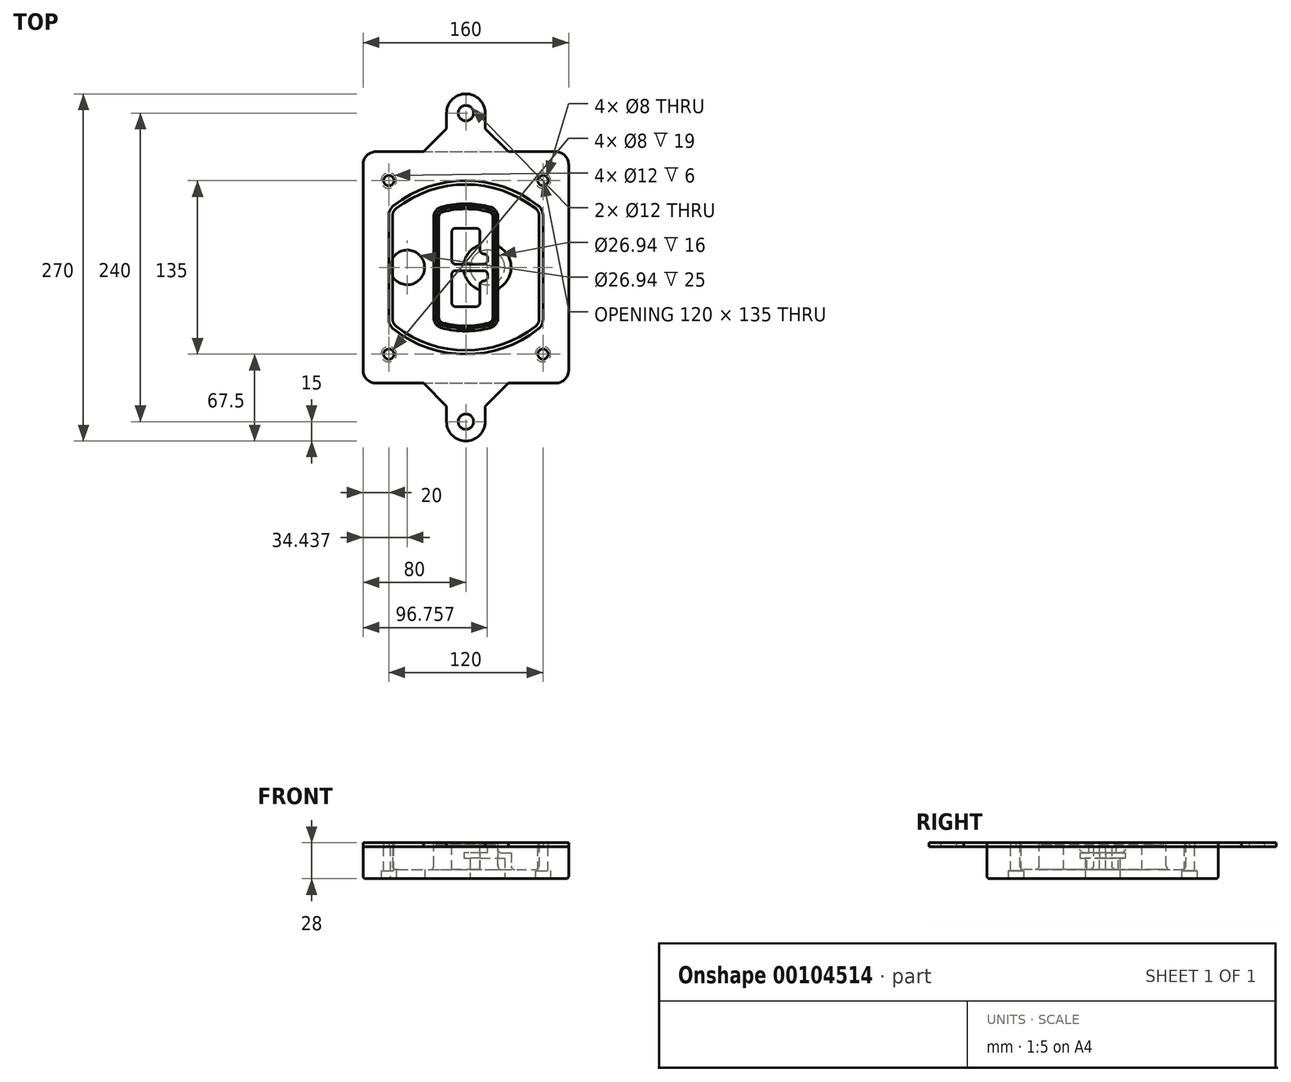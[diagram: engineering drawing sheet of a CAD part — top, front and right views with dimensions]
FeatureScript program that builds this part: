
annotation { "Feature Type Name" : "Feature", "Feature Type Description" : "" }
export const myFeature = defineFeature(function(context is Context, id is Id, definition is map)
    precondition{}
    {
        {
            var Q0;
            Q0=qCreatedBy(makeId("Top.planeOp"),FACE);
            var sketch = newSketch(context, id + "F0", { "sketchPlane" : qUnion([Q0])});
            skPoint(sketch, "E0.rect.middle", {"position": v(0, 0) * mm});
            skLineSegment(sketch, "E1.bottom", {"start": v(-70, -90) * mm, "end": v(70, -90) * mm});
            skLineSegment(sketch, "E1.top", {"start": v(-70, 90) * mm, "end": v(70, 90) * mm});
            skLineSegment(sketch, "E1.left", {"start": v(-80, -80) * mm, "end": v(-80, 80) * mm});
            skLineSegment(sketch, "E1.right", {"start": v(80, -80) * mm, "end": v(80, 80) * mm});
            skLineSegment(sketch, "E2", {"start": v(-80, 90) * mm, "end": v(80, -90) * mm, "construction": true});
            skLineSegment(sketch, "E3", {"start": v(80, 90) * mm, "end": v(-80, -90) * mm, "construction": true});
            skCircle(sketch, "E4", {"center": v(-60, 67.5) * mm, "radius": 4 * mm});
            skCircle(sketch, "E5", {"center": v(60, 67.5) * mm, "radius": 4 * mm});
            skCircle(sketch, "E6", {"center": v(60, -67.5) * mm, "radius": 4 * mm});
            skCircle(sketch, "E7", {"center": v(-60, -67.5) * mm, "radius": 4 * mm});
            skLineSegment(sketch, "E8", {"start": v(-60, 67.5) * mm, "end": v(60, 67.5) * mm, "construction": true});
            skLineSegment(sketch, "E9", {"start": v(60, 67.5) * mm, "end": v(60, -67.5) * mm, "construction": true});
            skLineSegment(sketch, "E10", {"start": v(60, -67.5) * mm, "end": v(-60, -67.5) * mm, "construction": true});
            skLineSegment(sketch, "E11", {"start": v(-60, -67.5) * mm, "end": v(-60, 67.5) * mm, "construction": true});
            skLineSegment(sketch, "E12", {"start": v(-60, 40.3) * mm, "end": v(-60, -40.3) * mm});
            skLineSegment(sketch, "E13", {"start": v(60, 40.3) * mm, "end": v(60, -40.3) * mm});
            skArc(sketch, "E14", {"start": v(56.15, 48.18) * mm, "mid": v(0, 67.5) * mm, "end": v(-56.15, 48.18) * mm});
            skArc(sketch, "E15", {"start": v(-56.15, -48.18) * mm, "mid": v(0, -67.5) * mm, "end": v(56.15, -48.18) * mm});
            skLineSegment(sketch, "E16", {"start": v(-60, 0) * mm, "end": v(60, 0) * mm, "construction": true});
            skPoint(sketch, "E17.visualSharp", {"position": v(-60, -45) * mm});
            skArc(sketch, "E17.filletArc", {"start": v(-60, -40.3) * mm, "mid": v(-58.99, -44.68) * mm, "end": v(-56.15, -48.18) * mm});
            skPoint(sketch, "E18.visualSharp", {"position": v(-60, 45) * mm});
            skArc(sketch, "E18.filletArc", {"start": v(-56.15, 48.18) * mm, "mid": v(-58.99, 44.68) * mm, "end": v(-60, 40.3) * mm});
            skPoint(sketch, "E19.visualSharp", {"position": v(60, 45) * mm});
            skArc(sketch, "E19.filletArc", {"start": v(60, 40.3) * mm, "mid": v(58.99, 44.68) * mm, "end": v(56.15, 48.18) * mm});
            skPoint(sketch, "E20.visualSharp", {"position": v(60, -45) * mm});
            skArc(sketch, "E20.filletArc", {"start": v(56.15, -48.18) * mm, "mid": v(58.99, -44.68) * mm, "end": v(60, -40.3) * mm});
            skPoint(sketch, "E21.visualSharp", {"position": v(-80, 90) * mm});
            skArc(sketch, "E21.filletArc", {"start": v(-70, 90) * mm, "mid": v(-77.07, 87.07) * mm, "end": v(-80, 80) * mm});
            skPoint(sketch, "E22.visualSharp", {"position": v(80, 90) * mm});
            skArc(sketch, "E22.filletArc", {"start": v(80, 80) * mm, "mid": v(77.07, 87.07) * mm, "end": v(70, 90) * mm});
            skPoint(sketch, "E23.visualSharp", {"position": v(80, -90) * mm});
            skArc(sketch, "E23.filletArc", {"start": v(70, -90) * mm, "mid": v(77.07, -87.07) * mm, "end": v(80, -80) * mm});
            skPoint(sketch, "E24.visualSharp", {"position": v(-80, -90) * mm});
            skArc(sketch, "E24.filletArc", {"start": v(-80, -80) * mm, "mid": v(-77.07, -87.07) * mm, "end": v(-70, -90) * mm});
            skArc(sketch, "E25.0", {"start": v(57, 40.3) * mm, "mid": v(56.3, 43.36) * mm, "end": v(54.3, 45.81) * mm});
            skLineSegment(sketch, "E25.1", {"start": v(57, 40.3) * mm, "end": v(57, -40.3) * mm});
            skArc(sketch, "E25.2", {"start": v(54.3, -45.81) * mm, "mid": v(56.3, -43.36) * mm, "end": v(57, -40.3) * mm});
            skArc(sketch, "E25.3", {"start": v(-54.3, -45.81) * mm, "mid": v(0, -64.5) * mm, "end": v(54.3, -45.81) * mm});
            skArc(sketch, "E25.4", {"start": v(-57, -40.3) * mm, "mid": v(-56.3, -43.36) * mm, "end": v(-54.3, -45.81) * mm});
            skArc(sketch, "E25.5", {"start": v(54.3, 45.81) * mm, "mid": v(0, 64.5) * mm, "end": v(-54.3, 45.81) * mm});
            skLineSegment(sketch, "E25.6", {"start": v(-57, 40.3) * mm, "end": v(-57, -40.3) * mm});
            skArc(sketch, "E25.7", {"start": v(-54.3, 45.81) * mm, "mid": v(-56.3, 43.36) * mm, "end": v(-57, 40.3) * mm});
            skArc(sketch, "E26.0", {"start": v(-58.62, 51.33) * mm, "mid": v(-62.58, 46.43) * mm, "end": v(-64, 40.3) * mm});
            skArc(sketch, "E26.1", {"start": v(58.62, 51.33) * mm, "mid": v(0, 71.5) * mm, "end": v(-58.62, 51.33) * mm});
            skArc(sketch, "E26.2", {"start": v(64, 40.3) * mm, "mid": v(62.58, 46.43) * mm, "end": v(58.62, 51.33) * mm});
            skLineSegment(sketch, "E26.3", {"start": v(64, 40.3) * mm, "end": v(64, -40.3) * mm});
            skArc(sketch, "E26.4", {"start": v(58.62, -51.33) * mm, "mid": v(62.58, -46.43) * mm, "end": v(64, -40.3) * mm});
            skLineSegment(sketch, "E26.5", {"start": v(-64, 40.3) * mm, "end": v(-64, -40.3) * mm});
            skArc(sketch, "E26.6", {"start": v(-58.62, -51.33) * mm, "mid": v(0, -71.5) * mm, "end": v(58.62, -51.33) * mm});
            skArc(sketch, "E26.7", {"start": v(-64, -40.3) * mm, "mid": v(-62.58, -46.43) * mm, "end": v(-58.62, -51.33) * mm});
            skSolve(sketch);
        }
        {
            var Q0;
            Q0=makeQuery(id+"F0.imprint","IMPRINT",FACE,{"disambiguationData":[TD([[makeQuery(id+"F0.imprint","IMPRINT",EDGE,{"derivedFrom":sQuery(id+"F0.wireOp",EDGE,"E1.bottom")}),1.0]])]});
            var Q1;
            Q1=makeQuery(id+"F0.imprint","IMPRINT",FACE,{"disambiguationData":[TD([[makeQuery(id+"F0.imprint","IMPRINT",EDGE,{"derivedFrom":sQuery(id+"F0.wireOp",EDGE,"E12")}),1.0]])]});
            var Q2;
            Q2=makeQuery(id+"F0.imprint","IMPRINT",FACE,{"disambiguationData":[TD([[makeQuery(id+"F0.imprint","IMPRINT",EDGE,{"derivedFrom":sQuery(id+"F0.wireOp",EDGE,"E25.0")}),1.0]])]});
            var Q3;
            Q3=makeQuery(id+"F0.imprint","IMPRINT",FACE,{"disambiguationData":[TD([[makeQuery(id+"F0.imprint","IMPRINT",EDGE,{"derivedFrom":sQuery(id+"F0.wireOp",EDGE,"E12")}),-1.0]])]});
            extrude(context, id + "F1", {"entities" : qUnion([Q0, Q1, Q2, Q3]), "oppositeDirection" : true, "depth" : 25 * mm});
        }
        {
            var Q0;
            Q0=makeQuery(id+"F0.imprint","IMPRINT",FACE,{"disambiguationData":[TD([[makeQuery(id+"F0.imprint","IMPRINT",EDGE,{"derivedFrom":sQuery(id+"F0.wireOp",EDGE,"E12")}),1.0]])]});
            extrude(context, id + "F2", {"entities" : qUnion([Q0]), "operationType" : NewBodyOperationType.ADD, "depth" : 3 * mm});
        }
        {
            var Q0;
            Q0=makeQuery(id+"F0.imprint","IMPRINT",FACE,{"disambiguationData":[TD([[makeQuery(id+"F0.imprint","IMPRINT",EDGE,{"derivedFrom":sQuery(id+"F0.wireOp",EDGE,"E25.0")}),1.0]])]});
            extrude(context, id + "F3", {"entities" : qUnion([Q0]), "operationType" : NewBodyOperationType.REMOVE, "oppositeDirection" : true, "depth" : 18 * mm});
        }
        {
            var Q0;
            Q0=makeQuery(id+"F2.opExtrude","CAP_FACE",FACE,{"disambiguationData":[OSD([sQuery(id+"F0.wireOp",EDGE,"E12"),sQuery(id+"F0.wireOp",EDGE,"E13"),sQuery(id+"F0.wireOp",EDGE,"E14"),sQuery(id+"F0.wireOp",EDGE,"E15"),sQuery(id+"F0.wireOp",EDGE,"E17.filletArc"),sQuery(id+"F0.wireOp",EDGE,"E18.filletArc"),sQuery(id+"F0.wireOp",EDGE,"E19.filletArc"),sQuery(id+"F0.wireOp",EDGE,"E20.filletArc"),sQuery(id+"F0.wireOp",EDGE,"E25.0"),sQuery(id+"F0.wireOp",EDGE,"E25.1"),sQuery(id+"F0.wireOp",EDGE,"E25.2"),sQuery(id+"F0.wireOp",EDGE,"E25.3"),sQuery(id+"F0.wireOp",EDGE,"E25.4"),sQuery(id+"F0.wireOp",EDGE,"E25.5"),sQuery(id+"F0.wireOp",EDGE,"E25.6"),sQuery(id+"F0.wireOp",EDGE,"E25.7")])],"isStart":false});
            var sketch = newSketch(context, id + "F4", { "sketchPlane" : qUnion([Q0])});
            skArc(sketch, "E27.0", {"start": v(-19.08, -46.97) * mm, "mid": v(0, -49.5) * mm, "end": v(19.08, -46.97) * mm});
            skArc(sketch, "E28.0", {"start": v(19.08, 46.97) * mm, "mid": v(0, 49.5) * mm, "end": v(-19.08, 46.97) * mm});
            skLineSegment(sketch, "E29", {"start": v(-25, 39.25) * mm, "end": v(-25, -39.25) * mm});
            skLineSegment(sketch, "E30", {"start": v(25, 39.25) * mm, "end": v(25, -39.25) * mm});
            skLineSegment(sketch, "E31", {"start": v(-25, 45.1) * mm, "end": v(25, 45.1) * mm, "construction": true});
            skLineSegment(sketch, "E32", {"start": v(-25, -45.1) * mm, "end": v(25, -45.1) * mm, "construction": true});
            skPoint(sketch, "E33.visualSharp", {"position": v(-25, 45.1) * mm});
            skArc(sketch, "E33.filletArc", {"start": v(-19.08, 46.97) * mm, "mid": v(-23.35, 44.11) * mm, "end": v(-25, 39.25) * mm});
            skPoint(sketch, "E34.visualSharp", {"position": v(25, 45.1) * mm});
            skArc(sketch, "E34.filletArc", {"start": v(25, 39.25) * mm, "mid": v(23.35, 44.11) * mm, "end": v(19.08, 46.97) * mm});
            skPoint(sketch, "E35.visualSharp", {"position": v(25, -45.1) * mm});
            skArc(sketch, "E35.filletArc", {"start": v(19.08, -46.97) * mm, "mid": v(23.35, -44.11) * mm, "end": v(25, -39.25) * mm});
            skPoint(sketch, "E36.visualSharp", {"position": v(-25, -45.1) * mm});
            skArc(sketch, "E36.filletArc", {"start": v(-25, -39.25) * mm, "mid": v(-23.35, -44.11) * mm, "end": v(-19.08, -46.97) * mm});
            skArc(sketch, "E37.0", {"start": v(54.3, 45.81) * mm, "mid": v(0, 64.5) * mm, "end": v(-54.3, 45.81) * mm});
            skArc(sketch, "E37.1", {"start": v(-54.3, 45.81) * mm, "mid": v(-56.3, 43.36) * mm, "end": v(-57, 40.3) * mm});
            skLineSegment(sketch, "E37.2", {"start": v(-57, 40.3) * mm, "end": v(-57, -40.3) * mm});
            skArc(sketch, "E37.3", {"start": v(-57, -40.3) * mm, "mid": v(-56.3, -43.36) * mm, "end": v(-54.3, -45.81) * mm});
            skArc(sketch, "E37.4", {"start": v(-54.3, -45.81) * mm, "mid": v(0, -64.5) * mm, "end": v(54.3, -45.81) * mm});
            skArc(sketch, "E37.5", {"start": v(54.3, -45.81) * mm, "mid": v(56.3, -43.36) * mm, "end": v(57, -40.3) * mm});
            skLineSegment(sketch, "E37.6", {"start": v(57, 40.3) * mm, "end": v(57, -40.3) * mm});
            skArc(sketch, "E37.7", {"start": v(57, 40.3) * mm, "mid": v(56.3, 43.36) * mm, "end": v(54.3, 45.81) * mm});
            skLineSegment(sketch, "E38.0", {"start": v(23, 39.25) * mm, "end": v(23, -39.25) * mm});
            skArc(sketch, "E38.1", {"start": v(18.56, -45.04) * mm, "mid": v(21.76, -42.9) * mm, "end": v(23, -39.25) * mm});
            skArc(sketch, "E38.2", {"start": v(-18.56, -45.04) * mm, "mid": v(0, -47.5) * mm, "end": v(18.56, -45.04) * mm});
            skArc(sketch, "E38.3", {"start": v(-23, -39.25) * mm, "mid": v(-21.76, -42.9) * mm, "end": v(-18.56, -45.04) * mm});
            skLineSegment(sketch, "E38.4", {"start": v(-23, 39.25) * mm, "end": v(-23, -39.25) * mm});
            skArc(sketch, "E38.5", {"start": v(23, 39.25) * mm, "mid": v(21.76, 42.9) * mm, "end": v(18.56, 45.04) * mm});
            skArc(sketch, "E38.6", {"start": v(-18.56, 45.04) * mm, "mid": v(-21.76, 42.9) * mm, "end": v(-23, 39.25) * mm});
            skArc(sketch, "E38.7", {"start": v(18.56, 45.04) * mm, "mid": v(0, 47.5) * mm, "end": v(-18.56, 45.04) * mm});
            skArc(sketch, "E39.0", {"start": v(21, 39.25) * mm, "mid": v(20.18, 41.68) * mm, "end": v(18.04, 43.1) * mm});
            skLineSegment(sketch, "E39.1", {"start": v(21, 39.25) * mm, "end": v(21, -39.25) * mm});
            skArc(sketch, "E39.2", {"start": v(18.04, -43.1) * mm, "mid": v(20.18, -41.68) * mm, "end": v(21, -39.25) * mm});
            skArc(sketch, "E39.3", {"start": v(-18.04, -43.1) * mm, "mid": v(0, -45.5) * mm, "end": v(18.04, -43.1) * mm});
            skArc(sketch, "E39.4", {"start": v(-21, -39.25) * mm, "mid": v(-20.18, -41.68) * mm, "end": v(-18.04, -43.1) * mm});
            skArc(sketch, "E39.5", {"start": v(18.04, 43.1) * mm, "mid": v(0, 45.5) * mm, "end": v(-18.04, 43.1) * mm});
            skLineSegment(sketch, "E39.6", {"start": v(-21, 39.25) * mm, "end": v(-21, -39.25) * mm});
            skArc(sketch, "E39.7", {"start": v(-18.04, 43.1) * mm, "mid": v(-20.18, 41.68) * mm, "end": v(-21, 39.25) * mm});
            skLineSegment(sketch, "E40", {"start": v(-25, 0) * mm, "end": v(25, 0) * mm, "construction": true});
            skLineSegment(sketch, "E41", {"start": v(-11, 5.5) * mm, "end": v(-11, 27.5) * mm});
            skLineSegment(sketch, "E42", {"start": v(-8, 30.5) * mm, "end": v(8, 30.5) * mm});
            skLineSegment(sketch, "E43", {"start": v(11, 27.5) * mm, "end": v(11, 13.5) * mm});
            skLineSegment(sketch, "E44", {"start": v(14, 10.5) * mm, "end": v(14, 10.5) * mm});
            skLineSegment(sketch, "E45", {"start": v(17, 7.5) * mm, "end": v(17, 5.5) * mm});
            skLineSegment(sketch, "E46", {"start": v(14, 2.5) * mm, "end": v(-8, 2.5) * mm});
            skPoint(sketch, "E47.visualSharp", {"position": v(-11, 30.5) * mm});
            skArc(sketch, "E47.filletArc", {"start": v(-8, 30.5) * mm, "mid": v(-10.12, 29.62) * mm, "end": v(-11, 27.5) * mm});
            skPoint(sketch, "E48.visualSharp", {"position": v(11, 30.5) * mm});
            skArc(sketch, "E48.filletArc", {"start": v(11, 27.5) * mm, "mid": v(10.12, 29.62) * mm, "end": v(8, 30.5) * mm});
            skPoint(sketch, "E49.visualSharp", {"position": v(11, 10.5) * mm});
            skArc(sketch, "E49.filletArc", {"start": v(11, 13.5) * mm, "mid": v(11.88, 11.38) * mm, "end": v(14, 10.5) * mm});
            skPoint(sketch, "E50.visualSharp", {"position": v(17, 10.5) * mm});
            skArc(sketch, "E50.filletArc", {"start": v(17, 7.5) * mm, "mid": v(16.12, 9.62) * mm, "end": v(14, 10.5) * mm});
            skPoint(sketch, "E51.visualSharp", {"position": v(17, 2.5) * mm});
            skArc(sketch, "E51.filletArc", {"start": v(14, 2.5) * mm, "mid": v(16.12, 3.38) * mm, "end": v(17, 5.5) * mm});
            skPoint(sketch, "E52.visualSharp", {"position": v(-11, 2.5) * mm});
            skArc(sketch, "E52.filletArc", {"start": v(-11, 5.5) * mm, "mid": v(-10.12, 3.38) * mm, "end": v(-8, 2.5) * mm});
            skLineSegment(sketch, "E53.0.MirrorCS", {"start": v(14, -2.5) * mm, "end": v(-8, -2.5) * mm});
            skArc(sketch, "E54.0.MirrorCS", {"start": v(-11, -5.5) * mm, "mid": v(-10.12, -3.38) * mm, "end": v(-8, -2.5) * mm});
            skLineSegment(sketch, "E55.0.MirrorCS", {"start": v(-11, -5.5) * mm, "end": v(-11, -27.5) * mm});
            skArc(sketch, "E56.0.MirrorCS", {"start": v(-8, -30.5) * mm, "mid": v(-10.12, -29.62) * mm, "end": v(-11, -27.5) * mm});
            skLineSegment(sketch, "E57.0.MirrorCS", {"start": v(-8, -30.5) * mm, "end": v(8, -30.5) * mm});
            skArc(sketch, "E58.0.MirrorCS", {"start": v(11, -27.5) * mm, "mid": v(10.12, -29.62) * mm, "end": v(8, -30.5) * mm});
            skLineSegment(sketch, "E59.0.MirrorCS", {"start": v(11, -27.5) * mm, "end": v(11, -13.5) * mm});
            skArc(sketch, "E60.0.MirrorCS", {"start": v(11, -13.5) * mm, "mid": v(11.88, -11.38) * mm, "end": v(14, -10.5) * mm});
            skArc(sketch, "E61.0.MirrorCS", {"start": v(17, -7.5) * mm, "mid": v(16.12, -9.62) * mm, "end": v(14, -10.5) * mm});
            skLineSegment(sketch, "E62.0.MirrorCS", {"start": v(17, -7.5) * mm, "end": v(17, -5.5) * mm});
            skArc(sketch, "E63.0.MirrorCS", {"start": v(14, -2.5) * mm, "mid": v(16.12, -3.38) * mm, "end": v(17, -5.5) * mm});
            skSolve(sketch);
        }
        {
            var Q0;
            Q0=makeQuery(id+"F4.imprint","IMPRINT",FACE,{"disambiguationData":[TD([[makeQuery(id+"F4.imprint","IMPRINT",EDGE,{"derivedFrom":sQuery(id+"F4.wireOp",EDGE,"E27.0")}),1.0]])]});
            var Q1;
            Q1=makeQuery(id+"F4.imprint","IMPRINT",FACE,{"disambiguationData":[TD([[makeQuery(id+"F4.imprint","IMPRINT",EDGE,{"derivedFrom":sQuery(id+"F4.wireOp",EDGE,"E38.0")}),-1.0]])]});
            var Q2;
            Q2=makeQuery(id+"F4.imprint","IMPRINT",FACE,{"disambiguationData":[TD([[makeQuery(id+"F4.imprint","IMPRINT",EDGE,{"derivedFrom":sQuery(id+"F4.wireOp",EDGE,"E39.0")}),1.0]])]});
            extrude(context, id + "F5", {"entities" : qUnion([Q0, Q1, Q2]), "operationType" : NewBodyOperationType.ADD, "endBound" : BoundingType.UP_TO_NEXT, "oppositeDirection" : true, "depth" : 25 * mm});
        }
        {
            var Q0;
            Q0=makeQuery(id+"F4.imprint","IMPRINT",FACE,{"disambiguationData":[TD([[makeQuery(id+"F4.imprint","IMPRINT",EDGE,{"derivedFrom":sQuery(id+"F4.wireOp",EDGE,"E38.0")}),-1.0]])]});
            extrude(context, id + "F6", {"entities" : qUnion([Q0]), "operationType" : NewBodyOperationType.REMOVE, "oppositeDirection" : true, "depth" : 2 * mm});
        }
        {
            var Q0;
            Q0=makeQuery(id+"F1.opExtrude","CAP_FACE",FACE,{"disambiguationData":[OSD([sQuery(id+"F0.wireOp",EDGE,"E1.bottom"),sQuery(id+"F0.wireOp",EDGE,"E1.top"),sQuery(id+"F0.wireOp",EDGE,"E1.left"),sQuery(id+"F0.wireOp",EDGE,"E1.right"),sQuery(id+"F0.wireOp",EDGE,"E4"),sQuery(id+"F0.wireOp",EDGE,"E5"),sQuery(id+"F0.wireOp",EDGE,"E6"),sQuery(id+"F0.wireOp",EDGE,"E7"),sQuery(id+"F0.wireOp",EDGE,"E21.filletArc"),sQuery(id+"F0.wireOp",EDGE,"E22.filletArc"),sQuery(id+"F0.wireOp",EDGE,"E23.filletArc"),sQuery(id+"F0.wireOp",EDGE,"E24.filletArc")])],"isStart":false});
            var sketch = newSketch(context, id + "F7", { "sketchPlane" : qUnion([Q0])});
            skCircle(sketch, "E64", {"center": v(16.76, 0) * mm, "radius": 13.47 * mm});
            skCircle(sketch, "E65", {"center": v(-45.56, 0) * mm, "radius": 13.47 * mm});
            skLineSegment(sketch, "E66", {"start": v(80, 0) * mm, "end": v(-80, 0) * mm});
            skCircle(sketch, "E67", {"center": v(16.76, 0) * mm, "radius": 18.47 * mm});
            skCircle(sketch, "E68", {"center": v(60, -67.5) * mm, "radius": 6 * mm});
            skCircle(sketch, "E69", {"center": v(-60, -67.5) * mm, "radius": 6 * mm});
            skCircle(sketch, "E70", {"center": v(-60, 67.5) * mm, "radius": 6 * mm});
            skCircle(sketch, "E71", {"center": v(60, 67.5) * mm, "radius": 6 * mm});
            skSolve(sketch);
        }
        {
            var Q0;
            {var subQ1=sQuery(id+"F7.wireOp",EDGE,"E66");var subQ4=sQuery(id+"F7.wireOp",EDGE,"E64");var subQ6=makeQuery(id+"F7.imprint","INTERSECT",VERTEX,{"disambiguationData":[OD(0.0)],"derivedFrom":[subQ4,subQ1]});Q0=makeQuery(id+"F7.imprint","IMPRINT",FACE,{"disambiguationData":[TD([[makeQuery(id+"F7.imprint","IMPRINT",EDGE,{"disambiguationData":[TD([[subQ6,-1.0]])],"derivedFrom":subQ4}),-1.0]])]});}
            var Q1;
            {var subQ0=sQuery(id+"F7.wireOp",EDGE,"E66");var subQ1=sQuery(id+"F7.wireOp",EDGE,"E64");var subQ3=makeQuery(id+"F7.imprint","INTERSECT",VERTEX,{"disambiguationData":[OD(0.0)],"derivedFrom":[subQ1,subQ0]});Q1=makeQuery(id+"F7.imprint","IMPRINT",FACE,{"disambiguationData":[TD([[makeQuery(id+"F7.imprint","IMPRINT",EDGE,{"disambiguationData":[TD([[subQ3,-1.0]])],"derivedFrom":subQ1}),1.0]])]});}
            var Q2;
            {var subQ0=sQuery(id+"F7.wireOp",EDGE,"E66");var subQ1=sQuery(id+"F7.wireOp",EDGE,"E64");var subQ3=makeQuery(id+"F7.imprint","INTERSECT",VERTEX,{"disambiguationData":[OD(0.0)],"derivedFrom":[subQ1,subQ0]});Q2=makeQuery(id+"F7.imprint","IMPRINT",FACE,{"disambiguationData":[TD([[makeQuery(id+"F7.imprint","IMPRINT",EDGE,{"disambiguationData":[TD([[subQ3,1.0]])],"derivedFrom":subQ1}),1.0]])]});}
            var Q3;
            {var subQ1=sQuery(id+"F7.wireOp",EDGE,"E66");var subQ4=sQuery(id+"F7.wireOp",EDGE,"E64");var subQ6=makeQuery(id+"F7.imprint","INTERSECT",VERTEX,{"disambiguationData":[OD(0.0)],"derivedFrom":[subQ4,subQ1]});Q3=makeQuery(id+"F7.imprint","IMPRINT",FACE,{"disambiguationData":[TD([[makeQuery(id+"F7.imprint","IMPRINT",EDGE,{"disambiguationData":[TD([[subQ6,1.0]])],"derivedFrom":subQ4}),-1.0]])]});}
            extrude(context, id + "F8", {"entities" : qUnion([Q0, Q1, Q2, Q3]), "operationType" : NewBodyOperationType.ADD, "oppositeDirection" : true, "depth" : 20 * mm});
        }
        {
            var Q0;
            {var subQ0=sQuery(id+"F7.wireOp",EDGE,"E66");var subQ1=sQuery(id+"F7.wireOp",EDGE,"E64");var subQ3=makeQuery(id+"F7.imprint","INTERSECT",VERTEX,{"disambiguationData":[OD(0.0)],"derivedFrom":[subQ1,subQ0]});Q0=makeQuery(id+"F7.imprint","IMPRINT",FACE,{"disambiguationData":[TD([[makeQuery(id+"F7.imprint","IMPRINT",EDGE,{"disambiguationData":[TD([[subQ3,-1.0]])],"derivedFrom":subQ1}),1.0]])]});}
            var Q1;
            {var subQ0=sQuery(id+"F7.wireOp",EDGE,"E66");var subQ1=sQuery(id+"F7.wireOp",EDGE,"E64");var subQ3=makeQuery(id+"F7.imprint","INTERSECT",VERTEX,{"disambiguationData":[OD(0.0)],"derivedFrom":[subQ1,subQ0]});Q1=makeQuery(id+"F7.imprint","IMPRINT",FACE,{"disambiguationData":[TD([[makeQuery(id+"F7.imprint","IMPRINT",EDGE,{"disambiguationData":[TD([[subQ3,1.0]])],"derivedFrom":subQ1}),1.0]])]});}
            extrude(context, id + "F9", {"entities" : qUnion([Q0, Q1]), "operationType" : NewBodyOperationType.REMOVE, "oppositeDirection" : true, "depth" : 16 * mm});
        }
        {
            var Q0;
            {var subQ0=sQuery(id+"F7.wireOp",EDGE,"E66");var subQ1=sQuery(id+"F7.wireOp",EDGE,"E65");var subQ3=makeQuery(id+"F7.imprint","INTERSECT",VERTEX,{"disambiguationData":[OD(0.0)],"derivedFrom":[subQ1,subQ0]});Q0=makeQuery(id+"F7.imprint","IMPRINT",FACE,{"disambiguationData":[TD([[makeQuery(id+"F7.imprint","IMPRINT",EDGE,{"disambiguationData":[TD([[subQ3,-1.0]])],"derivedFrom":subQ1}),1.0]])]});}
            var Q1;
            {var subQ0=sQuery(id+"F7.wireOp",EDGE,"E66");var subQ1=sQuery(id+"F7.wireOp",EDGE,"E65");var subQ3=makeQuery(id+"F7.imprint","INTERSECT",VERTEX,{"disambiguationData":[OD(0.0)],"derivedFrom":[subQ1,subQ0]});Q1=makeQuery(id+"F7.imprint","IMPRINT",FACE,{"disambiguationData":[TD([[makeQuery(id+"F7.imprint","IMPRINT",EDGE,{"disambiguationData":[TD([[subQ3,1.0]])],"derivedFrom":subQ1}),1.0]])]});}
            extrude(context, id + "F10", {"entities" : qUnion([Q0, Q1]), "operationType" : NewBodyOperationType.REMOVE, "oppositeDirection" : true, "depth" : 25 * mm});
        }
        {
            var Q0;
            Q0=makeQuery(id+"F7.imprint","IMPRINT",FACE,{"disambiguationData":[TD([[makeQuery(id+"F7.imprint","IMPRINT",EDGE,{"derivedFrom":sQuery(id+"F7.wireOp",EDGE,"E68")}),1.0]])]});
            var Q1;
            Q1=makeQuery(id+"F7.imprint","IMPRINT",FACE,{"disambiguationData":[TD([[makeQuery(id+"F7.imprint","IMPRINT",EDGE,{"derivedFrom":makeQuery(id+"F1.opExtrude","CAP_EDGE",EDGE,{"disambiguationData":[OSD([sQuery(id+"F0.wireOp",EDGE,"E5")])],"isStart":false})}),-1.0]])]});
            var Q2;
            Q2=makeQuery(id+"F7.imprint","IMPRINT",FACE,{"disambiguationData":[TD([[makeQuery(id+"F7.imprint","IMPRINT",EDGE,{"derivedFrom":sQuery(id+"F7.wireOp",EDGE,"E69")}),1.0]])]});
            var Q3;
            Q3=makeQuery(id+"F7.imprint","IMPRINT",FACE,{"disambiguationData":[TD([[makeQuery(id+"F7.imprint","IMPRINT",EDGE,{"derivedFrom":makeQuery(id+"F1.opExtrude","CAP_EDGE",EDGE,{"disambiguationData":[OSD([sQuery(id+"F0.wireOp",EDGE,"E4")])],"isStart":false})}),-1.0]])]});
            var Q4;
            Q4=makeQuery(id+"F7.imprint","IMPRINT",FACE,{"disambiguationData":[TD([[makeQuery(id+"F7.imprint","IMPRINT",EDGE,{"derivedFrom":sQuery(id+"F7.wireOp",EDGE,"E70")}),1.0]])]});
            var Q5;
            Q5=makeQuery(id+"F7.imprint","IMPRINT",FACE,{"disambiguationData":[TD([[makeQuery(id+"F7.imprint","IMPRINT",EDGE,{"derivedFrom":makeQuery(id+"F1.opExtrude","CAP_EDGE",EDGE,{"disambiguationData":[OSD([sQuery(id+"F0.wireOp",EDGE,"E7")])],"isStart":false})}),-1.0]])]});
            var Q6;
            Q6=makeQuery(id+"F7.imprint","IMPRINT",FACE,{"disambiguationData":[TD([[makeQuery(id+"F7.imprint","IMPRINT",EDGE,{"derivedFrom":sQuery(id+"F7.wireOp",EDGE,"E71")}),1.0]])]});
            var Q7;
            Q7=makeQuery(id+"F7.imprint","IMPRINT",FACE,{"disambiguationData":[TD([[makeQuery(id+"F7.imprint","IMPRINT",EDGE,{"derivedFrom":makeQuery(id+"F1.opExtrude","CAP_EDGE",EDGE,{"disambiguationData":[OSD([sQuery(id+"F0.wireOp",EDGE,"E6")])],"isStart":false})}),-1.0]])]});
            extrude(context, id + "F11", {"entities" : qUnion([Q0, Q1, Q2, Q3, Q4, Q5, Q6, Q7]), "operationType" : NewBodyOperationType.REMOVE, "oppositeDirection" : true, "depth" : 6 * mm});
        }
        {
            var Q0;
            Q0=makeQuery(id+"F9.boolean.opBoolean","COPY",FACE,{"derivedFrom":makeQuery(id+"F9.opExtrude","CAP_FACE",FACE,{"disambiguationData":[OSD([sQuery(id+"F7.wireOp",EDGE,"E64")])],"isStart":false})});
            var sketch = newSketch(context, id + "F12", { "sketchPlane" : qUnion([Q0])});
            skArc(sketch, "E72.0", {"start": v(11, 17.55) * mm, "mid": v(2.57, 11.82) * mm, "end": v(-1.54, 2.5) * mm});
            skArc(sketch, "E72.1", {"start": v(-1.54, -2.5) * mm, "mid": v(2.57, -11.82) * mm, "end": v(11, -17.55) * mm});
            skLineSegment(sketch, "E73", {"start": v(-1.54, -2.5) * mm, "end": v(14, -2.5) * mm});
            skLineSegment(sketch, "E74.0", {"start": v(14, 2.5) * mm, "end": v(-1.54, 2.5) * mm});
            skArc(sketch, "E74.1", {"start": v(14, 2.5) * mm, "mid": v(16.12, 3.38) * mm, "end": v(17, 5.5) * mm});
            skLineSegment(sketch, "E74.2", {"start": v(17, 7.5) * mm, "end": v(17, 5.5) * mm});
            skArc(sketch, "E74.3", {"start": v(17, 7.5) * mm, "mid": v(16.12, 9.62) * mm, "end": v(14, 10.5) * mm});
            skArc(sketch, "E74.4", {"start": v(11, 13.5) * mm, "mid": v(11.88, 11.38) * mm, "end": v(14, 10.5) * mm});
            skLineSegment(sketch, "E74.5", {"start": v(11, 17.55) * mm, "end": v(11, 13.5) * mm});
            skLineSegment(sketch, "E74.7", {"start": v(14, -2.5) * mm, "end": v(-1.54, -2.5) * mm});
            skArc(sketch, "E74.8", {"start": v(14, -2.5) * mm, "mid": v(16.12, -3.38) * mm, "end": v(17, -5.5) * mm});
            skLineSegment(sketch, "E74.9", {"start": v(17, -7.5) * mm, "end": v(17, -5.5) * mm});
            skArc(sketch, "E74.10", {"start": v(17, -7.5) * mm, "mid": v(16.12, -9.62) * mm, "end": v(14, -10.5) * mm});
            skArc(sketch, "E74.11", {"start": v(11, -13.5) * mm, "mid": v(11.88, -11.38) * mm, "end": v(14, -10.5) * mm});
            skLineSegment(sketch, "E74.12", {"start": v(11, -17.55) * mm, "end": v(11, -13.5) * mm});
            skPoint(sketch, "E75.orphan", {"position": v(11, -27.5) * mm});
            skPoint(sketch, "E76.orphan", {"position": v(-8, -2.5) * mm});
            skPoint(sketch, "E77.orphan", {"position": v(-8, 2.5) * mm});
            skPoint(sketch, "E78.orphan", {"position": v(11, 27.5) * mm});
            skSolve(sketch);
        }
        {
            var Q0;
            {var subQ7=sQuery(id+"F12.wireOp",EDGE,"E72.0");var subQ14=sQuery(id+"F12.wireOp",EDGE,"E72.1");var subQ16=sQuery(id+"F12.wireOp",EDGE,"E74.1");var subQ18=sQuery(id+"F12.wireOp",EDGE,"E74.8");Q0=qUnion([makeQuery(id+"F12.imprint","IMPRINT",FACE,{"disambiguationData":[TD([[makeQuery(id+"F12.imprint","IMPRINT",EDGE,{"derivedFrom":subQ7}),1.0]])]}),makeQuery(id+"F12.imprint","IMPRINT",FACE,{"disambiguationData":[TD([[makeQuery(id+"F12.imprint","IMPRINT",EDGE,{"derivedFrom":subQ14}),1.0]])]}),makeQuery(id+"F12.imprint","IMPRINT",FACE,{"disambiguationData":[TD([[makeQuery(id+"F12.imprint","IMPRINT",EDGE,{"derivedFrom":subQ16}),1.0]])]}),makeQuery(id+"F12.imprint","IMPRINT",FACE,{"disambiguationData":[TD([[makeQuery(id+"F12.imprint","IMPRINT",EDGE,{"derivedFrom":subQ18}),-1.0]])]})]);}
            var Q1;
            Q1=makeQuery(id+"F5.boolean.opBoolean","SPLIT",FACE,{"disambiguationData":[TD([makeQuery(id+"F5.opExtrude","SWEPT_FACE",FACE,{"disambiguationData":[OSD([sQuery(id+"F4.wireOp",EDGE,"E41")])]})])],"derivedFrom":makeQuery(id+"F3.boolean.opBoolean","COPY",FACE,{"derivedFrom":makeQuery(id+"F3.opExtrude","CAP_FACE",FACE,{"disambiguationData":[OSD([sQuery(id+"F0.wireOp",EDGE,"E25.0"),sQuery(id+"F0.wireOp",EDGE,"E25.1"),sQuery(id+"F0.wireOp",EDGE,"E25.2"),sQuery(id+"F0.wireOp",EDGE,"E25.3"),sQuery(id+"F0.wireOp",EDGE,"E25.4"),sQuery(id+"F0.wireOp",EDGE,"E25.5"),sQuery(id+"F0.wireOp",EDGE,"E25.6"),sQuery(id+"F0.wireOp",EDGE,"E25.7")])],"isStart":false})})});
            extrude(context, id + "F13", {"entities" : qUnion([Q0]), "operationType" : NewBodyOperationType.REMOVE, "endBound" : BoundingType.UP_TO_SURFACE, "endBoundEntityFace" : qUnion([Q1]), "depth" : 25 * mm});
        }
        {
            var Q0;
            Q0=makeQuery(id+"F3.boolean.opBoolean","COPY",EDGE,{"derivedFrom":makeQuery(id+"F3.opExtrude","CAP_EDGE",EDGE,{"disambiguationData":[OSD([sQuery(id+"F0.wireOp",EDGE,"E25.6")])],"isStart":false})});
            var Q1;
            Q1=makeQuery(id+"F8.boolean.opBoolean","INTERSECT",EDGE,{"derivedFrom":[makeQuery(id+"F5.opExtrude","SWEPT_FACE",FACE,{"disambiguationData":[OSD([sQuery(id+"F4.wireOp",EDGE,"E30")])]}),makeQuery(id+"F8.opExtrude","CAP_FACE",FACE,{"disambiguationData":[OSD([sQuery(id+"F7.wireOp",EDGE,"E67")])],"isStart":false})]});
            var Q2;
            Q2=makeQuery(id+"F8.boolean.opBoolean","INTERSECT",EDGE,{"disambiguationData":[OD(1.0)],"derivedFrom":[makeQuery(id+"F5.opExtrude","SWEPT_FACE",FACE,{"disambiguationData":[OSD([sQuery(id+"F4.wireOp",EDGE,"E30")])]}),makeQuery(id+"F8.opExtrude","SWEPT_FACE",FACE,{"disambiguationData":[OSD([sQuery(id+"F7.wireOp",EDGE,"E67")])]})]});
            var Q3;
            {var subQ0=sQuery(id+"F4.wireOp",EDGE,"E30");Q3=makeQuery(id+"F8.boolean.opBoolean","SPLIT",EDGE,{"disambiguationData":[TD([makeQuery(id+"F5.opExtrude","SWEPT_FACE",FACE,{"disambiguationData":[OSD([sQuery(id+"F4.wireOp",EDGE,"E35.filletArc")])]})])],"derivedFrom":makeQuery(id+"F5.opExtrude","CAP_EDGE",EDGE,{"disambiguationData":[OSD([subQ0])],"isStart":false})});}
            var Q4;
            {var subQ0=sQuery(id+"F0.wireOp",EDGE,"E25.7");var subQ1=sQuery(id+"F0.wireOp",EDGE,"E25.1");var subQ2=sQuery(id+"F0.wireOp",EDGE,"E25.6");var subQ3=sQuery(id+"F0.wireOp",EDGE,"E25.5");var subQ4=sQuery(id+"F0.wireOp",EDGE,"E25.4");var subQ5=sQuery(id+"F0.wireOp",EDGE,"E25.0");var subQ6=sQuery(id+"F0.wireOp",EDGE,"E25.2");var subQ7=sQuery(id+"F0.wireOp",EDGE,"E25.3");Q4=makeQuery(id+"F8.boolean.opBoolean","INTERSECT",EDGE,{"derivedFrom":[makeQuery(id+"F5.boolean.opBoolean","SPLIT",FACE,{"disambiguationData":[TD([makeQuery(id+"F2.opExtrude","SWEPT_FACE",FACE,{"disambiguationData":[OSD([subQ5])]})])],"derivedFrom":makeQuery(id+"F3.boolean.opBoolean","COPY",FACE,{"derivedFrom":makeQuery(id+"F3.opExtrude","CAP_FACE",FACE,{"disambiguationData":[OSD([subQ5,subQ1,subQ6,subQ7,subQ4,subQ3,subQ2,subQ0])],"isStart":false})})}),makeQuery(id+"F8.opExtrude","SWEPT_FACE",FACE,{"disambiguationData":[OSD([sQuery(id+"F7.wireOp",EDGE,"E67")])]})]});}
            var Q5;
            Q5=makeQuery(id+"F8.boolean.opBoolean","INTERSECT",EDGE,{"disambiguationData":[OD(0.0)],"derivedFrom":[makeQuery(id+"F5.opExtrude","SWEPT_FACE",FACE,{"disambiguationData":[OSD([sQuery(id+"F4.wireOp",EDGE,"E30")])]}),makeQuery(id+"F8.opExtrude","SWEPT_FACE",FACE,{"disambiguationData":[OSD([sQuery(id+"F7.wireOp",EDGE,"E67")])]})]});
            fillet(context, id + "F14", {"entities" : qUnion([Q0, Q1, Q2, Q3, Q4, Q5]), "radius" : 3 * mm, "tangentPropagation" : true, "allowEdgeOverflow" : false});
        }
        {
            var Q0;
            Q0=makeQuery(id+"F1.opExtrude","CAP_EDGE",EDGE,{"disambiguationData":[OSD([sQuery(id+"F0.wireOp",EDGE,"E1.bottom")])],"isStart":false});
            fillet(context, id + "F15", {"entities" : qUnion([Q0]), "radius" : 2 * mm, "tangentPropagation" : true, "allowEdgeOverflow" : false});
        }
        {
            var Q0;
            {var subQ0=sQuery(id+"F0.wireOp",EDGE,"E22.filletArc");var subQ1=sQuery(id+"F0.wireOp",EDGE,"E7");var subQ2=sQuery(id+"F0.wireOp",EDGE,"E6");var subQ3=sQuery(id+"F0.wireOp",EDGE,"E5");var subQ4=sQuery(id+"F0.wireOp",EDGE,"E4");var subQ5=sQuery(id+"F0.wireOp",EDGE,"E1.bottom");var subQ6=sQuery(id+"F0.wireOp",EDGE,"E21.filletArc");var subQ7=sQuery(id+"F0.wireOp",EDGE,"E1.top");var subQ8=sQuery(id+"F0.wireOp",EDGE,"E1.left");var subQ9=sQuery(id+"F0.wireOp",EDGE,"E1.right");var subQ10=sQuery(id+"F0.wireOp",EDGE,"E23.filletArc");var subQ11=sQuery(id+"F0.wireOp",EDGE,"E24.filletArc");Q0=makeQuery(id+"F2.boolean.opBoolean","SPLIT",FACE,{"disambiguationData":[TD([makeQuery(id+"F1.opExtrude","SWEPT_FACE",FACE,{"disambiguationData":[OSD([subQ5])]})])],"derivedFrom":makeQuery(id+"F1.opExtrude","CAP_FACE",FACE,{"disambiguationData":[OSD([subQ5,subQ7,subQ8,subQ9,subQ4,subQ3,subQ2,subQ1,subQ6,subQ0,subQ10,subQ11])],"isStart":true})});}
            var sketch = newSketch(context, id + "F16", { "sketchPlane" : qUnion([Q0])});
            skSolve(sketch);
        }
        {
            var Q0;
            {var subQ4=sQuery(id+"F0.wireOp",EDGE,"E1.bottom");Q0=makeQuery(id+"F16.imprint","IMPRINT",FACE,{"disambiguationData":[TD([[makeQuery(id+"F16.imprint","IMPRINT",EDGE,{"derivedFrom":makeQuery(id+"F1.opExtrude","CAP_EDGE",EDGE,{"disambiguationData":[OSD([subQ4])],"isStart":true})}),1.0]])]});}
            var sketch = newSketch(context, id + "F17", { "sketchPlane" : qUnion([Q0])});
            skLineSegment(sketch, "E79.0", {"start": v(-80, -80) * mm, "end": v(-80, 80) * mm});
            skArc(sketch, "E79.1", {"start": v(-70, 90) * mm, "mid": v(-77.07, 87.07) * mm, "end": v(-80, 80) * mm});
            skLineSegment(sketch, "E79.2", {"start": v(-70, 90) * mm, "end": v(70, 90) * mm});
            skArc(sketch, "E79.3", {"start": v(80, 80) * mm, "mid": v(77.07, 87.07) * mm, "end": v(70, 90) * mm});
            skLineSegment(sketch, "E79.4", {"start": v(80, -80) * mm, "end": v(80, 80) * mm});
            skArc(sketch, "E79.5", {"start": v(70, -90) * mm, "mid": v(77.07, -87.07) * mm, "end": v(80, -80) * mm});
            skLineSegment(sketch, "E79.6", {"start": v(-70, -90) * mm, "end": v(70, -90) * mm});
            skArc(sketch, "E79.7", {"start": v(-80, -80) * mm, "mid": v(-77.07, -87.07) * mm, "end": v(-70, -90) * mm});
            skCircle(sketch, "E79.8", {"center": v(-60, -67.5) * mm, "radius": 4 * mm});
            skCircle(sketch, "E79.9", {"center": v(60, -67.5) * mm, "radius": 4 * mm});
            skCircle(sketch, "E79.10", {"center": v(60, 67.5) * mm, "radius": 4 * mm});
            skCircle(sketch, "E79.11", {"center": v(-60, 67.5) * mm, "radius": 4 * mm});
            skArc(sketch, "E79.12", {"start": v(56.15, 48.18) * mm, "mid": v(0, 67.5) * mm, "end": v(-56.15, 48.18) * mm});
            skArc(sketch, "E79.13", {"start": v(60, 40.3) * mm, "mid": v(58.99, 44.68) * mm, "end": v(56.15, 48.18) * mm});
            skLineSegment(sketch, "E79.14", {"start": v(60, 40.3) * mm, "end": v(60, -40.3) * mm});
            skArc(sketch, "E79.15", {"start": v(56.15, -48.18) * mm, "mid": v(58.99, -44.68) * mm, "end": v(60, -40.3) * mm});
            skArc(sketch, "E79.16", {"start": v(-56.15, -48.18) * mm, "mid": v(0, -67.5) * mm, "end": v(56.15, -48.18) * mm});
            skArc(sketch, "E79.17", {"start": v(-60, -40.3) * mm, "mid": v(-58.99, -44.68) * mm, "end": v(-56.15, -48.18) * mm});
            skLineSegment(sketch, "E79.18", {"start": v(-60, 40.3) * mm, "end": v(-60, -40.3) * mm});
            skArc(sketch, "E79.19", {"start": v(-56.15, 48.18) * mm, "mid": v(-58.99, 44.68) * mm, "end": v(-60, 40.3) * mm});
            skLineSegment(sketch, "E80", {"start": v(0, 120) * mm, "end": v(0, 90) * mm, "construction": true});
            skLineSegment(sketch, "E81", {"start": v(-33, 90) * mm, "end": v(-15, 108) * mm});
            skLineSegment(sketch, "E82", {"start": v(-15, 108) * mm, "end": v(-15, 120) * mm});
            skLineSegment(sketch, "E83", {"start": v(15, 120) * mm, "end": v(15, 108) * mm});
            skLineSegment(sketch, "E84", {"start": v(15, 108) * mm, "end": v(33, 90) * mm});
            skCircle(sketch, "E85", {"center": v(0, 120) * mm, "radius": 6 * mm});
            skArc(sketch, "E86", {"start": v(15, 120) * mm, "mid": v(0, 135) * mm, "end": v(-15, 120) * mm});
            skLineSegment(sketch, "E87", {"start": v(80, 0) * mm, "end": v(-80, 0) * mm, "construction": true});
            skLineSegment(sketch, "E88.MirrorCS", {"start": v(-33, -90) * mm, "end": v(-15, -108) * mm});
            skLineSegment(sketch, "E89.MirrorCS", {"start": v(-15, -108) * mm, "end": v(-15, -120) * mm});
            skArc(sketch, "E90.MirrorCS", {"start": v(15, -120) * mm, "mid": v(0, -135) * mm, "end": v(-15, -120) * mm});
            skLineSegment(sketch, "E91.MirrorCS", {"start": v(15, -120) * mm, "end": v(15, -108) * mm});
            skLineSegment(sketch, "E92.MirrorCS", {"start": v(15, -108) * mm, "end": v(33, -90) * mm});
            skLineSegment(sketch, "E93.MirrorCS", {"start": v(0, -120) * mm, "end": v(0, -90) * mm, "construction": true});
            skCircle(sketch, "E94.MirrorC", {"center": v(0, -120) * mm, "radius": 6 * mm});
            skSolve(sketch);
        }
        {
            var Q0;
            Q0 = qSketchRegion(id + "F17", true);
            var Q1;
            Q1=makeQuery(id+"F2.opExtrude","CAP_FACE",FACE,{"disambiguationData":[OSD([sQuery(id+"F0.wireOp",EDGE,"E12"),sQuery(id+"F0.wireOp",EDGE,"E13"),sQuery(id+"F0.wireOp",EDGE,"E14"),sQuery(id+"F0.wireOp",EDGE,"E15"),sQuery(id+"F0.wireOp",EDGE,"E17.filletArc"),sQuery(id+"F0.wireOp",EDGE,"E18.filletArc"),sQuery(id+"F0.wireOp",EDGE,"E19.filletArc"),sQuery(id+"F0.wireOp",EDGE,"E20.filletArc"),sQuery(id+"F0.wireOp",EDGE,"E25.0"),sQuery(id+"F0.wireOp",EDGE,"E25.1"),sQuery(id+"F0.wireOp",EDGE,"E25.2"),sQuery(id+"F0.wireOp",EDGE,"E25.3"),sQuery(id+"F0.wireOp",EDGE,"E25.4"),sQuery(id+"F0.wireOp",EDGE,"E25.5"),sQuery(id+"F0.wireOp",EDGE,"E25.6"),sQuery(id+"F0.wireOp",EDGE,"E25.7")])],"isStart":false});
            extrude(context, id + "F18", {"entities" : qUnion([Q0]), "endBound" : BoundingType.UP_TO_SURFACE, "endBoundEntityFace" : qUnion([Q1]), "depth" : 25 * mm});
        }
    });
